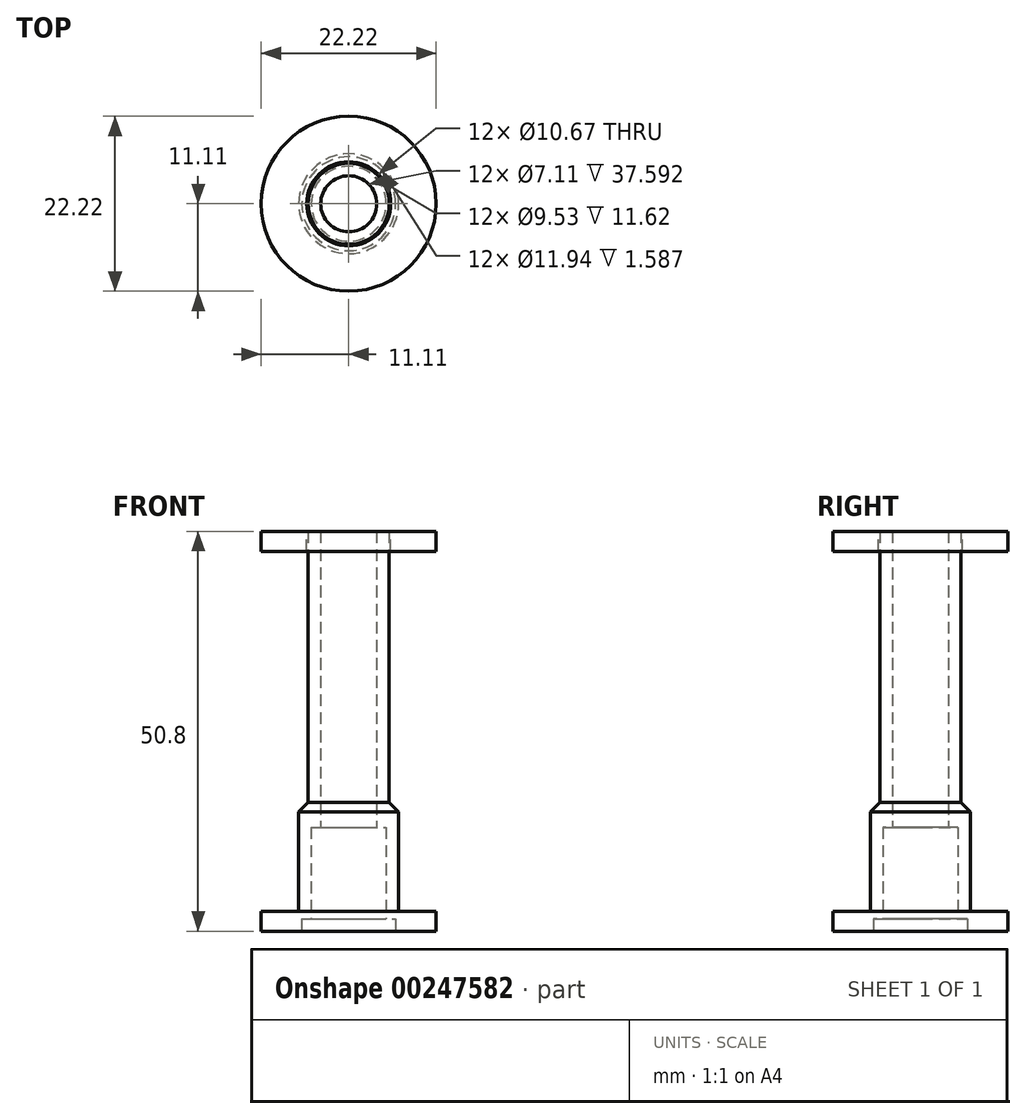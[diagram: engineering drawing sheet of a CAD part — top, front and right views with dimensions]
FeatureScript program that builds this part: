
annotation { "Feature Type Name" : "Feature", "Feature Type Description" : "" }
export const myFeature = defineFeature(function(context is Context, id is Id, definition is map)
    precondition{}
    {
        {
            var Q0;
            Q0=qCreatedBy(makeId("Right.planeOp"),FACE);
            var sketch = newSketch(context, id + "F0", { "sketchPlane" : qUnion([Q0])});
            skLineSegment(sketch, "E0", {"start": v(4.76, 13.2) * mm, "end": v(4.76, 1.59) * mm});
            skLineSegment(sketch, "E1", {"start": v(4.76, 1.59) * mm, "end": v(5.97, 1.59) * mm});
            skLineSegment(sketch, "E2", {"start": v(5.97, 1.59) * mm, "end": v(5.97, 0) * mm});
            skLineSegment(sketch, "E3", {"start": v(5.97, 0) * mm, "end": v(11.11, 0) * mm});
            skLineSegment(sketch, "E4", {"start": v(11.11, 0) * mm, "end": v(11.11, 2.54) * mm});
            skLineSegment(sketch, "E5", {"start": v(11.11, 2.54) * mm, "end": v(6.35, 2.54) * mm});
            skLineSegment(sketch, "E6", {"start": v(5.14, 50.8) * mm, "end": v(3.56, 50.8) * mm});
            skLineSegment(sketch, "E7", {"start": v(3.56, 50.8) * mm, "end": v(3.56, 13.2) * mm});
            skLineSegment(sketch, "E8", {"start": v(3.56, 13.2) * mm, "end": v(4.76, 13.2) * mm});
            skLineSegment(sketch, "E9", {"start": v(6.35, 2.54) * mm, "end": v(6.35, 14.8) * mm});
            skLineSegment(sketch, "E10", {"start": v(6.35, 14.8) * mm, "end": v(5.14, 14.8) * mm});
            skLineSegment(sketch, "E11", {"start": v(5.14, 14.8) * mm, "end": v(5.14, 50.8) * mm});
            skLineSegment(sketch, "E12", {"start": v(0, 0) * mm, "end": v(0, 54.6) * mm});
            skSolve(sketch);
        }
        {
            var Q0;
            Q0 = qSketchRegion(id + "F0", true);
            var Q1;
            Q1=sQuery(id+"F0.wireOp",EDGE,"E12");
            revolve(context, id + "F1", {"entities" : qUnion([Q0]), "axis" : qUnion([Q1]), "revolveType" : RevolveType.FULL});
        }
        {
            var Q0;
            Q0=makeQuery(id+"F1.opRevolve","SWEPT_FACE",FACE,{"disambiguationData":[OSD([sQuery(id+"F0.wireOp",EDGE,"E6")])]});
            var sketch = newSketch(context, id + "F2", { "sketchPlane" : qUnion([Q0])});
            skCircle(sketch, "E13.0", {"center": v(0, 0) * mm, "radius": 11.11 * mm});
            skCircle(sketch, "E14.0", {"center": v(0, 0) * mm, "radius": 5.14 * mm});
            skSolve(sketch);
        }
        {
            var Q0;
            Q0 = qSketchRegion(id + "F2", true);
            extrude(context, id + "F3", {"entities" : qUnion([Q0]), "oppositeDirection" : true, "depth" : 2.54 * mm});
        }
        {
            var Q0;
            Q0=makeQuery(id+"F1.opRevolve","SWEPT_EDGE",EDGE,{"disambiguationData":[OSD([sQuery(id+"F0.wireOp",EDGE,"E10"),sQuery(id+"F0.wireOp",EDGE,"E11")])]});
            chamfer(context, id + "F4", {"entities" : qUnion([Q0]), "width" : 1.59 * mm, "tangentPropagation" : true});
        }
        {
            var Q0;
            Q0=makeQuery(id+"F3.opExtrude","CAP_FACE",FACE,{"disambiguationData":[OSD([sQuery(id+"F2.wireOp",EDGE,"E13.0"),sQuery(id+"F2.wireOp",EDGE,"E14.0")])],"isStart":true});
            var sketch = newSketch(context, id + "F5", { "sketchPlane" : qUnion([Q0])});
            skCircle(sketch, "E15.0", {"center": v(0, 0) * mm, "radius": 5.14 * mm});
            skCircle(sketch, "E16.0", {"center": v(0, 0) * mm, "radius": 5.33 * mm});
            skSolve(sketch);
        }
        {
            var Q0;
            Q0 = qSketchRegion(id + "F5", true);
            extrude(context, id + "F6", {"entities" : qUnion([Q0]), "operationType" : NewBodyOperationType.REMOVE, "endBound" : BoundingType.UP_TO_NEXT, "oppositeDirection" : true, "depth" : 25.4 * mm});
        }
    });
